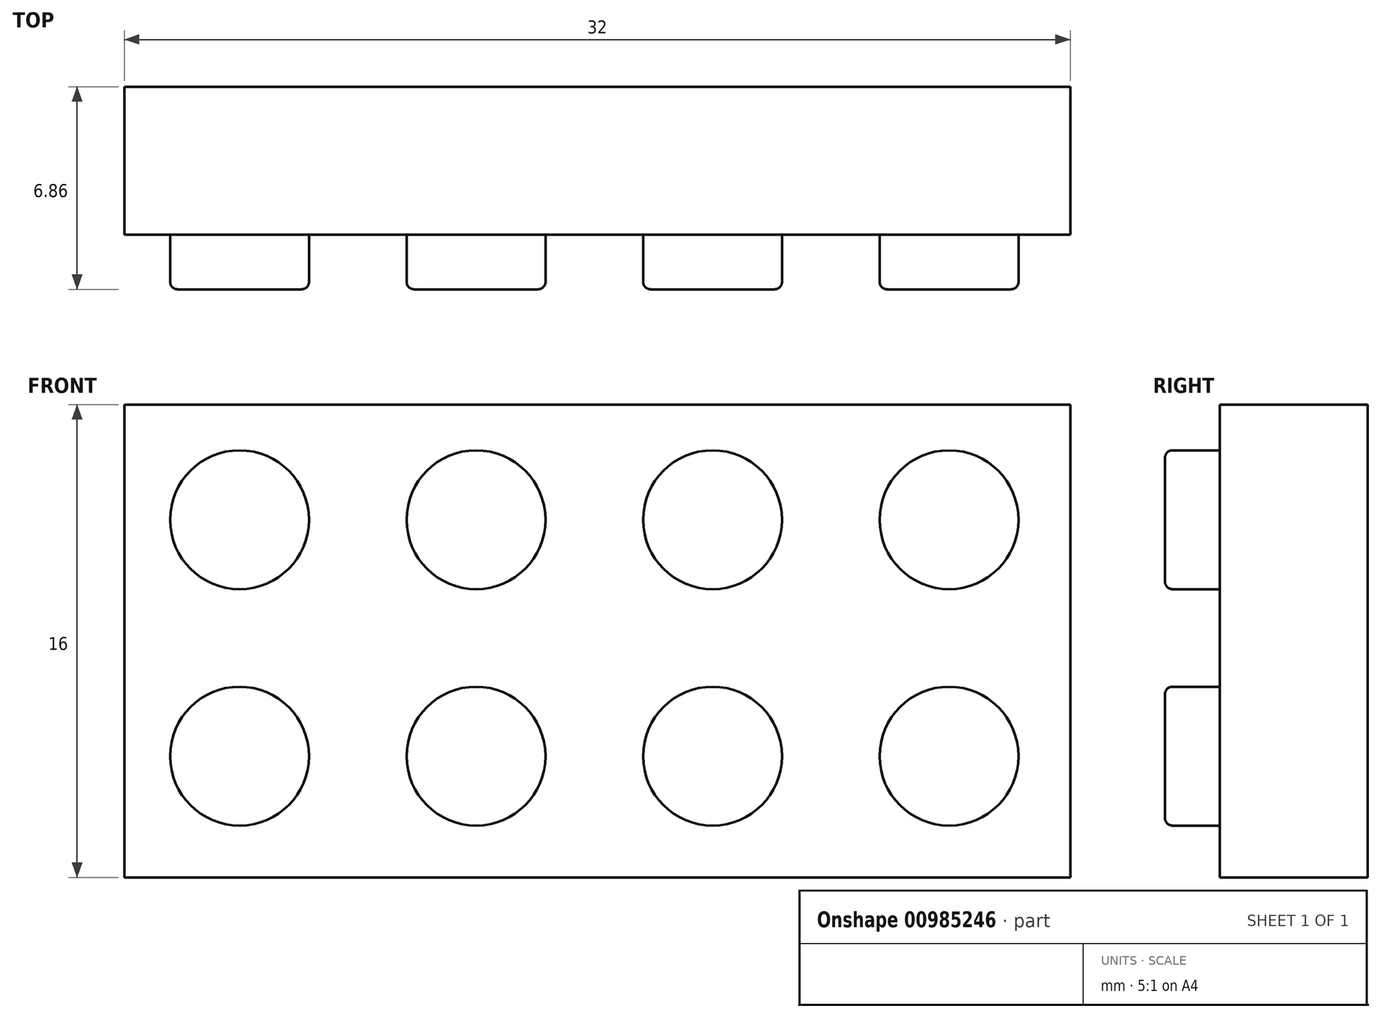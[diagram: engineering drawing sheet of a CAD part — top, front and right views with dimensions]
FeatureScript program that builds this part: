
annotation { "Feature Type Name" : "Feature", "Feature Type Description" : "" }
export const myFeature = defineFeature(function(context is Context, id is Id, definition is map)
    precondition{}
    {
        {
            var Q0;
            Q0=qCreatedBy(makeId("Front.planeOp"),FACE);
            var sketch = newSketch(context, id + "F0", { "sketchPlane" : qUnion([Q0])});
            skLineSegment(sketch, "E0.bottom", {"start": v(0, 0) * mm, "end": v(-32, 0) * mm});
            skLineSegment(sketch, "E0.top", {"start": v(0, 16) * mm, "end": v(-32, 16) * mm});
            skLineSegment(sketch, "E0.left", {"start": v(0, 0) * mm, "end": v(0, 16) * mm});
            skLineSegment(sketch, "E0.right", {"start": v(-32, 0) * mm, "end": v(-32, 16) * mm});
            skSolve(sketch);
        }
        {
            var Q0;
            Q0=makeQuery(id+"F0.imprint","IMPRINT",FACE,{"disambiguationData":[TD([[makeQuery(id+"F0.imprint","IMPRINT",EDGE,{"derivedFrom":sQuery(id+"F0.wireOp",EDGE,"E0.bottom")}),-1.0]])]});
            extrude(context, id + "F1", {"entities" : qUnion([Q0]), "depth" : 5 * mm, "offsetDistance" : 25.4 * mm});
        }
        {
            var Q0;
            Q0=makeQuery(id+"F1.opExtrude","CAP_FACE",FACE,{"disambiguationData":[OSD([sQuery(id+"F0.wireOp",EDGE,"E0.bottom"),sQuery(id+"F0.wireOp",EDGE,"E0.top"),sQuery(id+"F0.wireOp",EDGE,"E0.left"),sQuery(id+"F0.wireOp",EDGE,"E0.right")])],"isStart":false});
            var sketch = newSketch(context, id + "F2", { "sketchPlane" : qUnion([Q0])});
            skCircle(sketch, "E1", {"center": v(-28.1, 12.1) * mm, "radius": 2.35 * mm});
            skCircle(sketch, "E2.0.1.0", {"center": v(-28.1, 4.1) * mm, "radius": 2.35 * mm});
            skCircle(sketch, "E2.1.0.0", {"center": v(-20.1, 12.1) * mm, "radius": 2.35 * mm});
            skCircle(sketch, "E2.1.1.0", {"center": v(-20.1, 4.1) * mm, "radius": 2.35 * mm});
            skCircle(sketch, "E2.2.0.0", {"center": v(-12.1, 12.1) * mm, "radius": 2.35 * mm});
            skCircle(sketch, "E2.2.1.0", {"center": v(-12.1, 4.1) * mm, "radius": 2.35 * mm});
            skCircle(sketch, "E2.3.0.0", {"center": v(-4.1, 12.1) * mm, "radius": 2.35 * mm});
            skCircle(sketch, "E2.3.1.0", {"center": v(-4.1, 4.1) * mm, "radius": 2.35 * mm});
            skLineSegment(sketch, "E2.direction1", {"start": v(-28.1, 12.1) * mm, "end": v(-20.1, 12.1) * mm, "construction": true});
            skLineSegment(sketch, "E2.direction2", {"start": v(-28.1, 12.1) * mm, "end": v(-28.1, 4.1) * mm, "construction": true});
            skSolve(sketch);
        }
        {
            var Q0;
            Q0=makeQuery(id+"F2.imprint","IMPRINT",FACE,{"disambiguationData":[TD([[makeQuery(id+"F2.imprint","IMPRINT",EDGE,{"derivedFrom":sQuery(id+"F2.wireOp",EDGE,"E1")}),1.0]])]});
            var Q1;
            Q1=makeQuery(id+"F2.imprint","IMPRINT",FACE,{"disambiguationData":[TD([[makeQuery(id+"F2.imprint","IMPRINT",EDGE,{"derivedFrom":sQuery(id+"F2.wireOp",EDGE,"E2.1.0.0")}),1.0]])]});
            var Q2;
            Q2=makeQuery(id+"F2.imprint","IMPRINT",FACE,{"disambiguationData":[TD([[makeQuery(id+"F2.imprint","IMPRINT",EDGE,{"derivedFrom":sQuery(id+"F2.wireOp",EDGE,"E2.2.0.0")}),1.0]])]});
            var Q3;
            Q3=makeQuery(id+"F2.imprint","IMPRINT",FACE,{"disambiguationData":[TD([[makeQuery(id+"F2.imprint","IMPRINT",EDGE,{"derivedFrom":sQuery(id+"F2.wireOp",EDGE,"E2.3.0.0")}),1.0]])]});
            var Q4;
            Q4=makeQuery(id+"F2.imprint","IMPRINT",FACE,{"disambiguationData":[TD([[makeQuery(id+"F2.imprint","IMPRINT",EDGE,{"derivedFrom":sQuery(id+"F2.wireOp",EDGE,"E2.0.1.0")}),1.0]])]});
            var Q5;
            Q5=makeQuery(id+"F2.imprint","IMPRINT",FACE,{"disambiguationData":[TD([[makeQuery(id+"F2.imprint","IMPRINT",EDGE,{"derivedFrom":sQuery(id+"F2.wireOp",EDGE,"E2.1.1.0")}),1.0]])]});
            var Q6;
            Q6=makeQuery(id+"F2.imprint","IMPRINT",FACE,{"disambiguationData":[TD([[makeQuery(id+"F2.imprint","IMPRINT",EDGE,{"derivedFrom":sQuery(id+"F2.wireOp",EDGE,"E2.2.1.0")}),1.0]])]});
            var Q7;
            Q7=makeQuery(id+"F2.imprint","IMPRINT",FACE,{"disambiguationData":[TD([[makeQuery(id+"F2.imprint","IMPRINT",EDGE,{"derivedFrom":sQuery(id+"F2.wireOp",EDGE,"E2.3.1.0")}),1.0]])]});
            extrude(context, id + "F3", {"entities" : qUnion([Q0, Q1, Q2, Q3, Q4, Q5, Q6, Q7]), "operationType" : NewBodyOperationType.ADD, "depth" : 1.85 * mm, "offsetDistance" : 25.4 * mm});
        }
        {
            var Q0;
            Q0=makeQuery(id+"F3.opExtrude","CAP_EDGE",EDGE,{"disambiguationData":[OSD([sQuery(id+"F2.wireOp",EDGE,"E1")])],"isStart":false});
            var Q1;
            Q1=makeQuery(id+"F3.opExtrude","CAP_EDGE",EDGE,{"disambiguationData":[OSD([sQuery(id+"F2.wireOp",EDGE,"E2.1.0.0")])],"isStart":false});
            var Q2;
            Q2=makeQuery(id+"F3.opExtrude","CAP_EDGE",EDGE,{"disambiguationData":[OSD([sQuery(id+"F2.wireOp",EDGE,"E2.2.0.0")])],"isStart":false});
            var Q3;
            Q3=makeQuery(id+"F3.opExtrude","CAP_EDGE",EDGE,{"disambiguationData":[OSD([sQuery(id+"F2.wireOp",EDGE,"E2.3.0.0")])],"isStart":false});
            var Q4;
            Q4=makeQuery(id+"F3.opExtrude","CAP_EDGE",EDGE,{"disambiguationData":[OSD([sQuery(id+"F2.wireOp",EDGE,"E2.0.1.0")])],"isStart":false});
            var Q5;
            Q5=makeQuery(id+"F3.opExtrude","CAP_EDGE",EDGE,{"disambiguationData":[OSD([sQuery(id+"F2.wireOp",EDGE,"E2.1.1.0")])],"isStart":false});
            var Q6;
            Q6=makeQuery(id+"F3.opExtrude","CAP_EDGE",EDGE,{"disambiguationData":[OSD([sQuery(id+"F2.wireOp",EDGE,"E2.2.1.0")])],"isStart":false});
            var Q7;
            Q7=makeQuery(id+"F3.opExtrude","CAP_EDGE",EDGE,{"disambiguationData":[OSD([sQuery(id+"F2.wireOp",EDGE,"E2.3.1.0")])],"isStart":false});
            fillet(context, id + "F4", {"entities" : qUnion([Q0, Q1, Q2, Q3, Q4, Q5, Q6, Q7]), "radius" : 0.25 * mm, "tangentPropagation" : true, "allowEdgeOverflow" : false});
        }
    });
